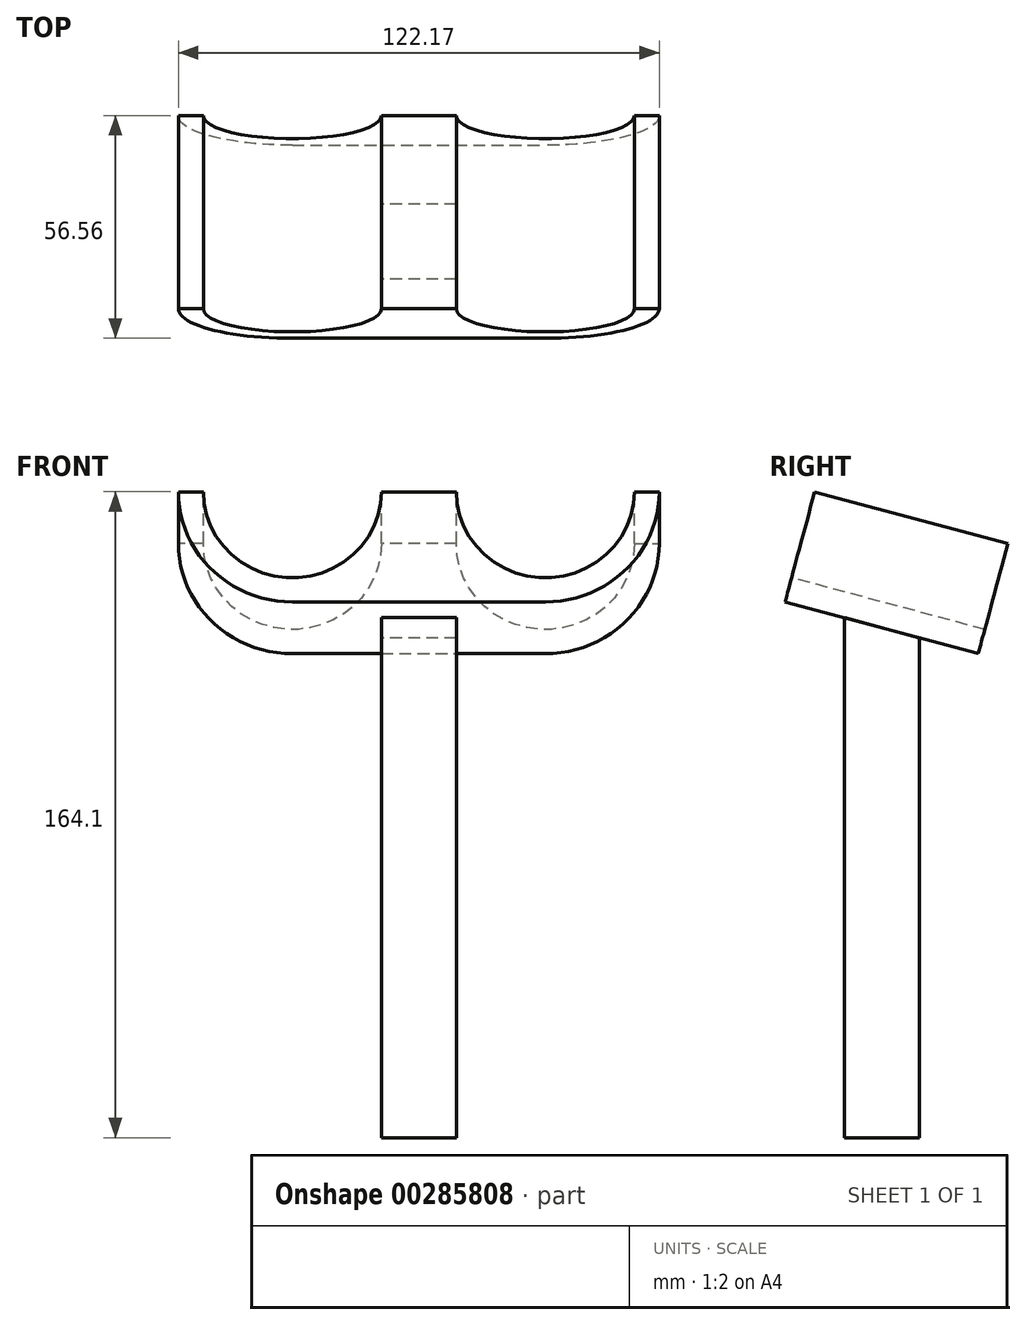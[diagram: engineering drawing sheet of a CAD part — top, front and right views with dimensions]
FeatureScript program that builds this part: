
annotation { "Feature Type Name" : "Feature", "Feature Type Description" : "" }
export const myFeature = defineFeature(function(context is Context, id is Id, definition is map)
    precondition{}
    {
        {
            var Q0;
            Q0=qCreatedBy(makeId("Right.planeOp"),FACE);
            var sketch = newSketch(context, id + "F0", { "sketchPlane" : qUnion([Q0])});
            skLineSegment(sketch, "E0.bottom", {"start": v(-9.52, -63.5) * mm, "end": v(9.53, -63.5) * mm});
            skLineSegment(sketch, "E0.left", {"start": v(-9.52, -63.5) * mm, "end": v(-9.53, 63.5) * mm});
            skLineSegment(sketch, "E0.right", {"start": v(9.53, -63.5) * mm, "end": v(9.52, 63.5) * mm});
            skPoint(sketch, "E0.middle", {"position": v(0, 0) * mm});
            skLineSegment(sketch, "E1", {"start": v(9.52, 63.5) * mm, "end": v(-9.53, 68.6) * mm});
            skLineSegment(sketch, "E2", {"start": v(40.67, 63.5) * mm, "end": v(-96.02, 63.5) * mm, "construction": true});
            skLineSegment(sketch, "E3", {"start": v(-9.53, 68.6) * mm, "end": v(-9.53, 63.5) * mm});
            skSolve(sketch);
        }
        {
            var Q0;
            Q0 = qSketchRegion(id + "F0", true);
            extrude(context, id + "F1", {"entities" : qUnion([Q0]), "depth" : 19.05 * mm});
        }
        {
            var Q0;
            Q0=makeQuery(id+"F1.opExtrude","SWEPT_FACE",FACE,{"disambiguationData":[OSD([sQuery(id+"F0.wireOp",EDGE,"E1")])]});
            var sketch = newSketch(context, id + "F2", { "sketchPlane" : qUnion([Q0])});
            skLineSegment(sketch, "E4", {"start": v(0, -17.1) * mm, "end": v(19.05, -17.1) * mm, "construction": true});
            skSolve(sketch);
        }
        {
            var Q0;
            Q0=sQuery(id+"F2.wireOp",EDGE,"E4");
            cPlane(context, id + "F3", {"entities" : qUnion([Q0]), "cplaneType" : CPlaneType.LINE_ANGLE, "offset" : 25.4 * mm, "angle" : 15 * degree, "oppositeDirection" : true, "width" : 152.4 * mm, "height" : 152.4 * mm});
        }
        {
            var Q0;
            Q0=qCreatedBy(id+"F3.planeOp",FACE);
            var sketch = newSketch(context, id + "F4", { "sketchPlane" : qUnion([Q0])});
            skLineSegment(sketch, "E5", {"start": v(-19.05, 63.8) * mm, "end": v(0, 63.8) * mm});
            skCircle(sketch, "E6", {"center": v(-41.66, 92.76) * mm, "radius": 22.6 * mm, "construction": true});
            skLineSegment(sketch, "E7", {"start": v(-9.53, 63.8) * mm, "end": v(-9.53, 115.21) * mm, "construction": true});
            skCircle(sketch, "E8.MirrorC", {"center": v(22.6, 92.76) * mm, "radius": 22.6 * mm, "construction": true});
            skLineSegment(sketch, "E9", {"start": v(-41.66, 92.76) * mm, "end": v(-19.05, 92.76) * mm, "construction": true});
            skLineSegment(sketch, "E10", {"start": v(-19.05, 92.76) * mm, "end": v(0, 92.76) * mm, "construction": true});
            skLineSegment(sketch, "E11", {"start": v(0, 92.76) * mm, "end": v(22.6, 92.76) * mm, "construction": true});
            skLineSegment(sketch, "E12", {"start": v(-19.05, 92.76) * mm, "end": v(0, 92.76) * mm});
            skLineSegment(sketch, "E13", {"start": v(-41.66, 92.76) * mm, "end": v(-41.66, 70.15) * mm, "construction": true});
            skLineSegment(sketch, "E14", {"start": v(22.6, 92.76) * mm, "end": v(22.6, 70.15) * mm, "construction": true});
            skLineSegment(sketch, "E15", {"start": v(-41.66, 70.15) * mm, "end": v(-41.66, 49.5) * mm, "construction": true});
            skLineSegment(sketch, "E16", {"start": v(22.6, 70.15) * mm, "end": v(22.6, 49.5) * mm, "construction": true});
            skLineSegment(sketch, "E17", {"start": v(0, 63.8) * mm, "end": v(22.6, 63.8) * mm});
            skLineSegment(sketch, "E18", {"start": v(-19.05, 63.8) * mm, "end": v(-41.66, 63.8) * mm});
            skArc(sketch, "E19", {"start": v(22.6, 63.8) * mm, "mid": v(43.08, 72.28) * mm, "end": v(51.56, 92.76) * mm});
            skArc(sketch, "E20", {"start": v(-41.66, 63.8) * mm, "mid": v(-62.13, 72.28) * mm, "end": v(-70.61, 92.76) * mm});
            skArc(sketch, "E21", {"start": v(-64.26, 92.76) * mm, "mid": v(-41.66, 70.15) * mm, "end": v(-19.05, 92.76) * mm});
            skArc(sketch, "E22", {"start": v(0, 92.76) * mm, "mid": v(22.6, 70.15) * mm, "end": v(45.21, 92.76) * mm});
            skLineSegment(sketch, "E23", {"start": v(-64.26, 92.76) * mm, "end": v(-70.61, 92.76) * mm});
            skLineSegment(sketch, "E24", {"start": v(45.21, 92.76) * mm, "end": v(51.56, 92.76) * mm});
            skSolve(sketch);
        }
        {
            var Q0;
            Q0 = qSketchRegion(id + "F4", true);
            extrude(context, id + "F5", {"entities" : qUnion([Q0]), "operationType" : NewBodyOperationType.ADD, "endBound" : BoundingType.SYMMETRIC, "depth" : 50.8 * mm});
        }
        {
            var Q0;
            Q0=makeQuery(id+"F1.opExtrude","SWEPT_BODY",BODY,{"disambiguationData":[OSD([sQuery(id+"F0.wireOp",EDGE,"E0.bottom"),sQuery(id+"F0.wireOp",EDGE,"E0.left"),sQuery(id+"F0.wireOp",EDGE,"E0.right"),sQuery(id+"F0.wireOp",EDGE,"E1"),sQuery(id+"F0.wireOp",EDGE,"E3")])]});
            transform(context, id + "F6", {"entities" : qUnion([Q0]), "transformType" : TransformType.TRANSLATION_3D, "dx" : 0 * mm, "dy" : 0 * mm, "dz" : 0 * mm, "makeCopy" : true});
        }
    });
